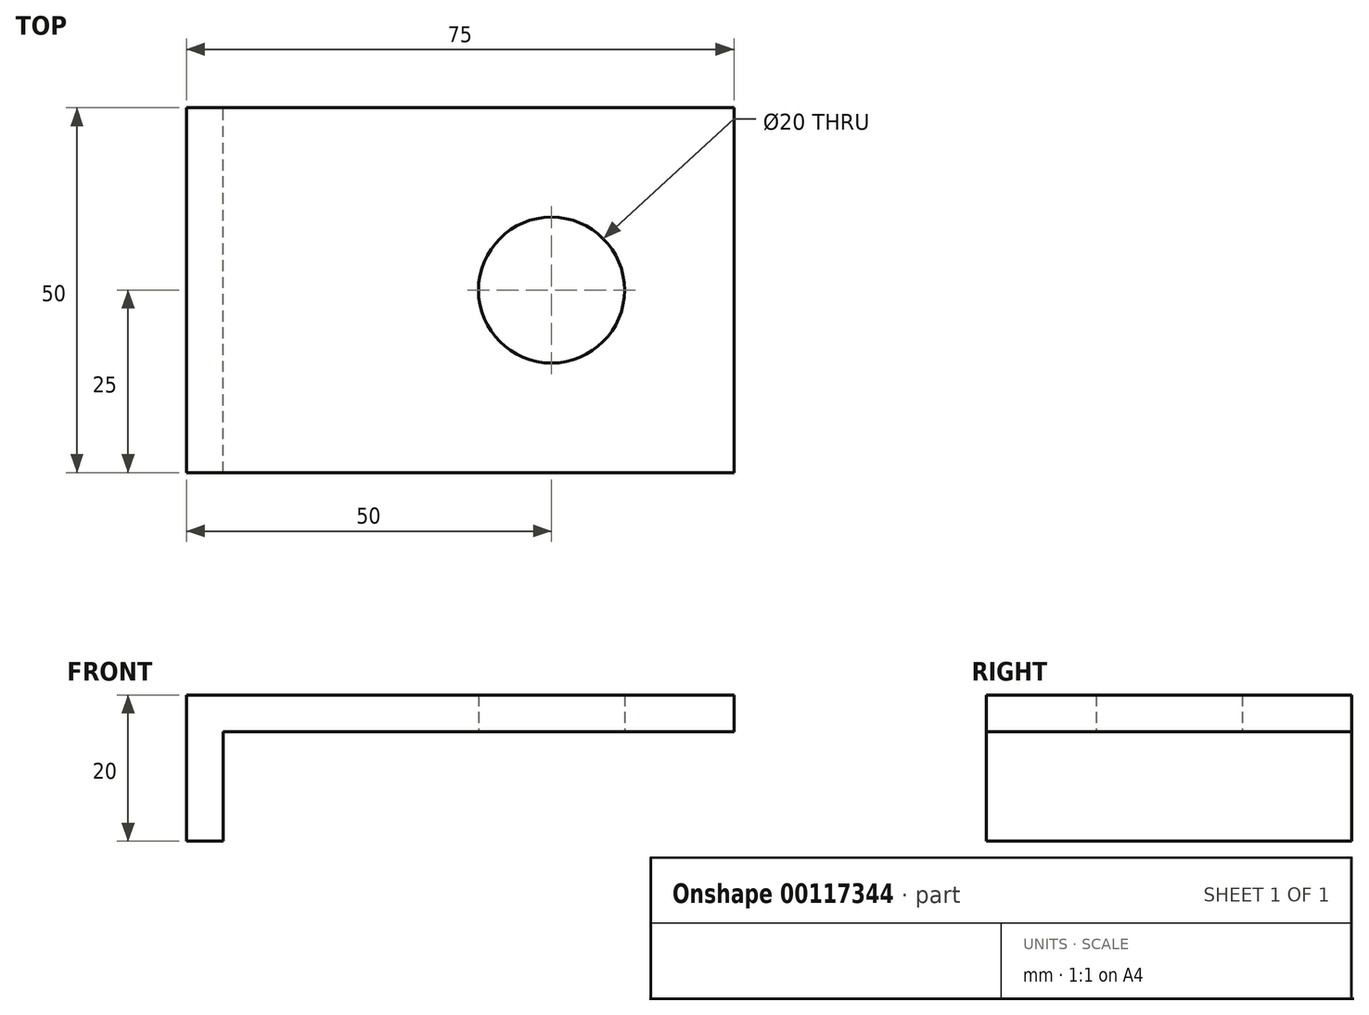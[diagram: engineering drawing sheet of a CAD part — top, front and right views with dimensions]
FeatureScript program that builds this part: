
annotation { "Feature Type Name" : "Feature", "Feature Type Description" : "" }
export const myFeature = defineFeature(function(context is Context, id is Id, definition is map)
    precondition{}
    {
        {
            var Q0;
            Q0=qCreatedBy(makeId("Front.planeOp"),FACE);
            var sketch = newSketch(context, id + "F0", { "sketchPlane" : qUnion([Q0])});
            skLineSegment(sketch, "E0", {"start": v(0, 0) * mm, "end": v(5, 0) * mm});
            skLineSegment(sketch, "E1", {"start": v(5, 0) * mm, "end": v(5, 15) * mm});
            skLineSegment(sketch, "E2", {"start": v(5, 15) * mm, "end": v(75, 15) * mm});
            skLineSegment(sketch, "E3", {"start": v(0, 0) * mm, "end": v(0, 20) * mm});
            skLineSegment(sketch, "E4", {"start": v(0, 20) * mm, "end": v(75, 20) * mm});
            skLineSegment(sketch, "E5", {"start": v(75, 20) * mm, "end": v(75, 15) * mm});
            skSolve(sketch);
        }
        {
            var Q0;
            Q0=qSketchRegion(id+"F0",true);
            extrude(context, id + "F1", {"entities" : qUnion([Q0]), "depth" : 50 * mm});
        }
        {
            var Q0;
            Q0=makeQuery(id+"F1.opExtrude","SWEPT_FACE",FACE,{"disambiguationData":[OSD([sQuery(id+"F0.wireOp",EDGE,"E2")])]});
            var sketch = newSketch(context, id + "F2", { "sketchPlane" : qUnion([Q0])});
            skCircle(sketch, "E6", {"center": v(50, 25) * mm, "radius": 10 * mm});
            skPoint(sketch, "E6.centerSnap0", {"position": v(75, 25) * mm});
            skSolve(sketch);
        }
        {
            var Q0;
            Q0 = qSketchRegion(id + "F2", true);
            extrude(context, id + "F3", {"entities" : qUnion([Q0]), "operationType" : NewBodyOperationType.REMOVE, "oppositeDirection" : true, "depth" : 25 * mm});
        }
    });
